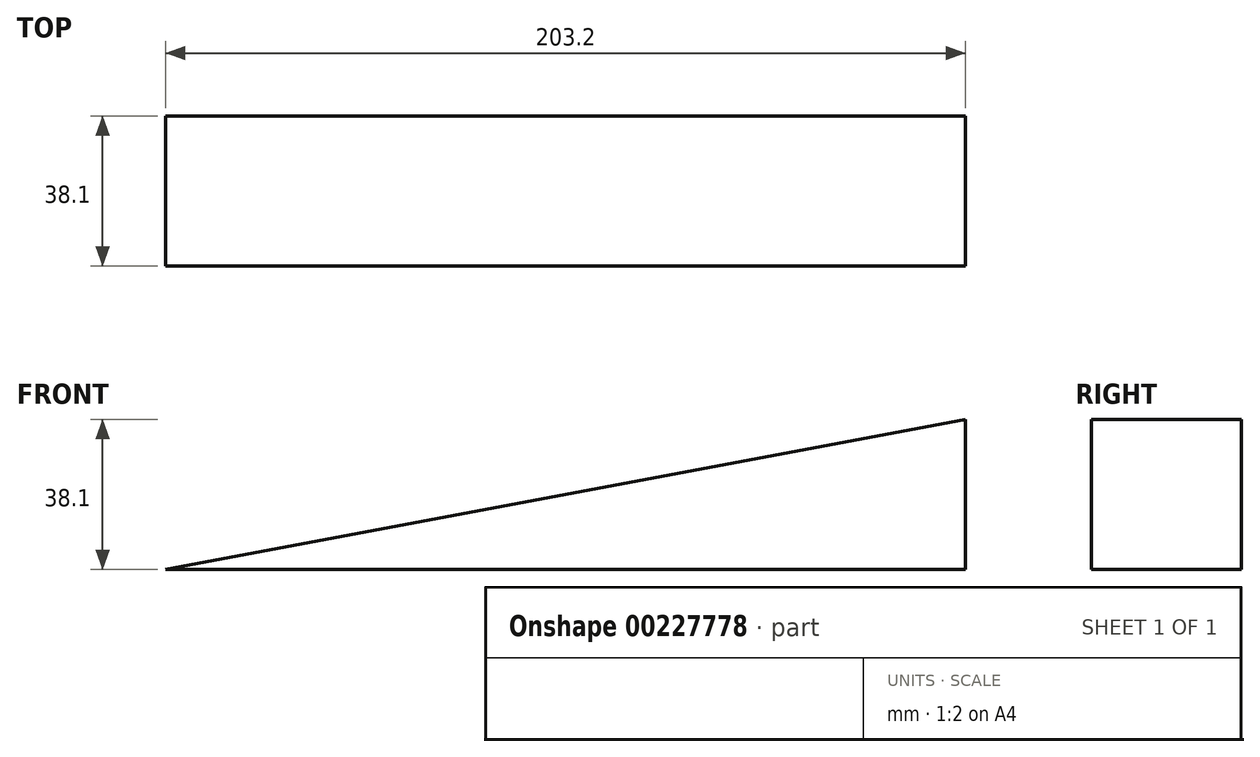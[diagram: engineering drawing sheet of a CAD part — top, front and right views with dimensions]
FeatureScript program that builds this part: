
annotation { "Feature Type Name" : "Feature", "Feature Type Description" : "" }
export const myFeature = defineFeature(function(context is Context, id is Id, definition is map)
    precondition{}
    {
        {
            var Q0;
            Q0=qCreatedBy(makeId("Front.planeOp"),FACE);
            var sketch = newSketch(context, id + "F0", { "sketchPlane" : qUnion([Q0])});
            skLineSegment(sketch, "E0", {"start": v(-105.99, 0) * mm, "end": v(97.21, 0) * mm});
            skLineSegment(sketch, "E1", {"start": v(97.21, 0) * mm, "end": v(97.21, 38.1) * mm});
            skLineSegment(sketch, "E2", {"start": v(97.21, 38.1) * mm, "end": v(-105.99, 0) * mm});
            skSolve(sketch);
        }
        {
            var Q0;
            Q0=makeQuery(id+"F0.imprint","IMPRINT",FACE,{"disambiguationData":[TD([[makeQuery(id+"F0.imprint","IMPRINT",EDGE,{"derivedFrom":sQuery(id+"F0.wireOp",EDGE,"E0")}),1.0]])]});
            extrude(context, id + "F1", {"entities" : qUnion([Q0]), "depth" : 38.1 * mm});
        }
    });
